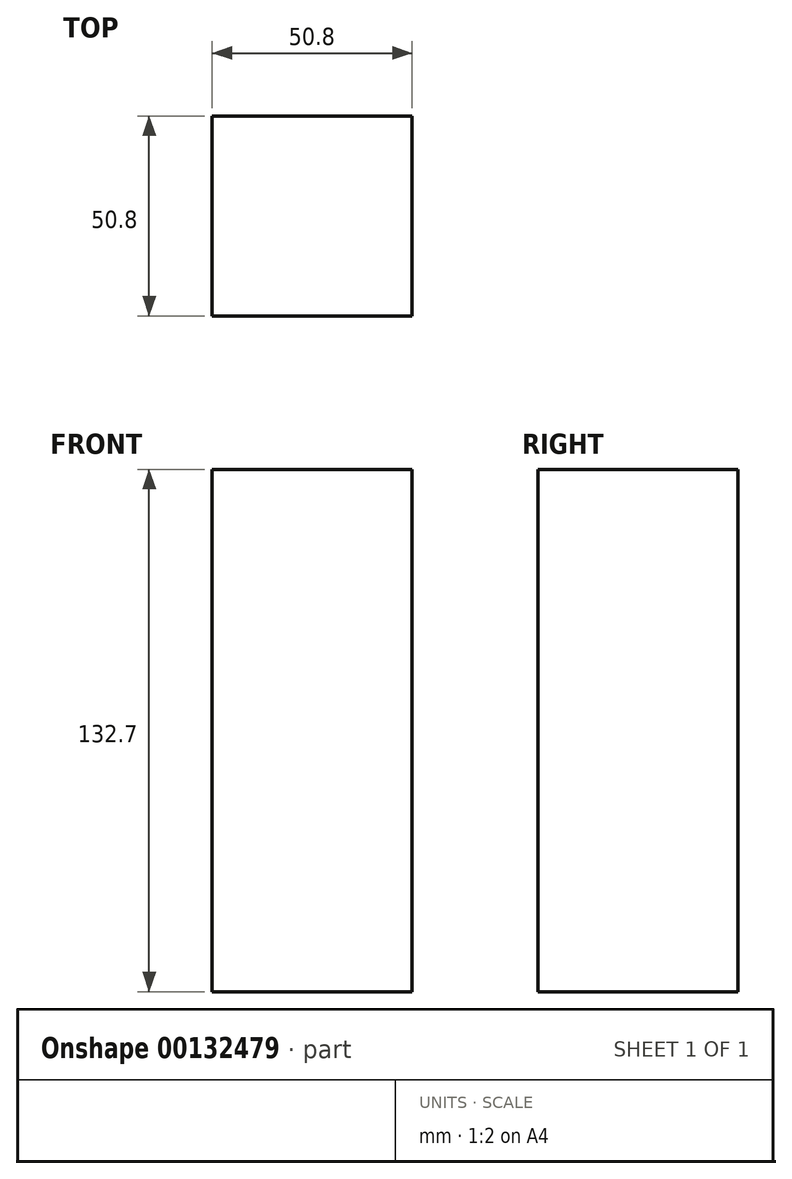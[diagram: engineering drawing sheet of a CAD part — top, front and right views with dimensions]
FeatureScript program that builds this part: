
annotation { "Feature Type Name" : "Feature", "Feature Type Description" : "" }
export const myFeature = defineFeature(function(context is Context, id is Id, definition is map)
    precondition{}
    {
        {
            var Q0;
            Q0=qCreatedBy(makeId("Front.planeOp"),FACE);
            var sketch = newSketch(context, id + "F0", { "sketchPlane" : qUnion([Q0])});
            skLineSegment(sketch, "E0", {"start": v(0, 0) * mm, "end": v(0, 50.8) * mm});
            skLineSegment(sketch, "E1", {"start": v(0, 50.8) * mm, "end": v(50.8, 50.8) * mm});
            skLineSegment(sketch, "E2", {"start": v(50.8, 50.8) * mm, "end": v(50.8, 0) * mm});
            skLineSegment(sketch, "E3", {"start": v(0, 0) * mm, "end": v(50.8, 0) * mm});
            skSolve(sketch);
        }
        {
            var Q0;
            Q0=makeQuery(id+"F0.imprint","IMPRINT",FACE,{"disambiguationData":[TD([[makeQuery(id+"F0.imprint","IMPRINT",EDGE,{"derivedFrom":sQuery(id+"F0.wireOp",EDGE,"E0")}),-1.0]])]});
            extrude(context, id + "F1", {"entities" : qUnion([Q0]), "endBound" : BoundingType.SYMMETRIC, "depth" : 50.8 * mm});
        }
        {
            var Q0;
            Q0=makeQuery(id+"F1.opExtrude","SWEPT_FACE",FACE,{"disambiguationData":[OSD([sQuery(id+"F0.wireOp",EDGE,"E1")])]});
            extrude(context, id + "F2", {"entities" : qUnion([Q0]), "operationType" : NewBodyOperationType.ADD, "depth" : 81.9 * mm});
        }
    });
